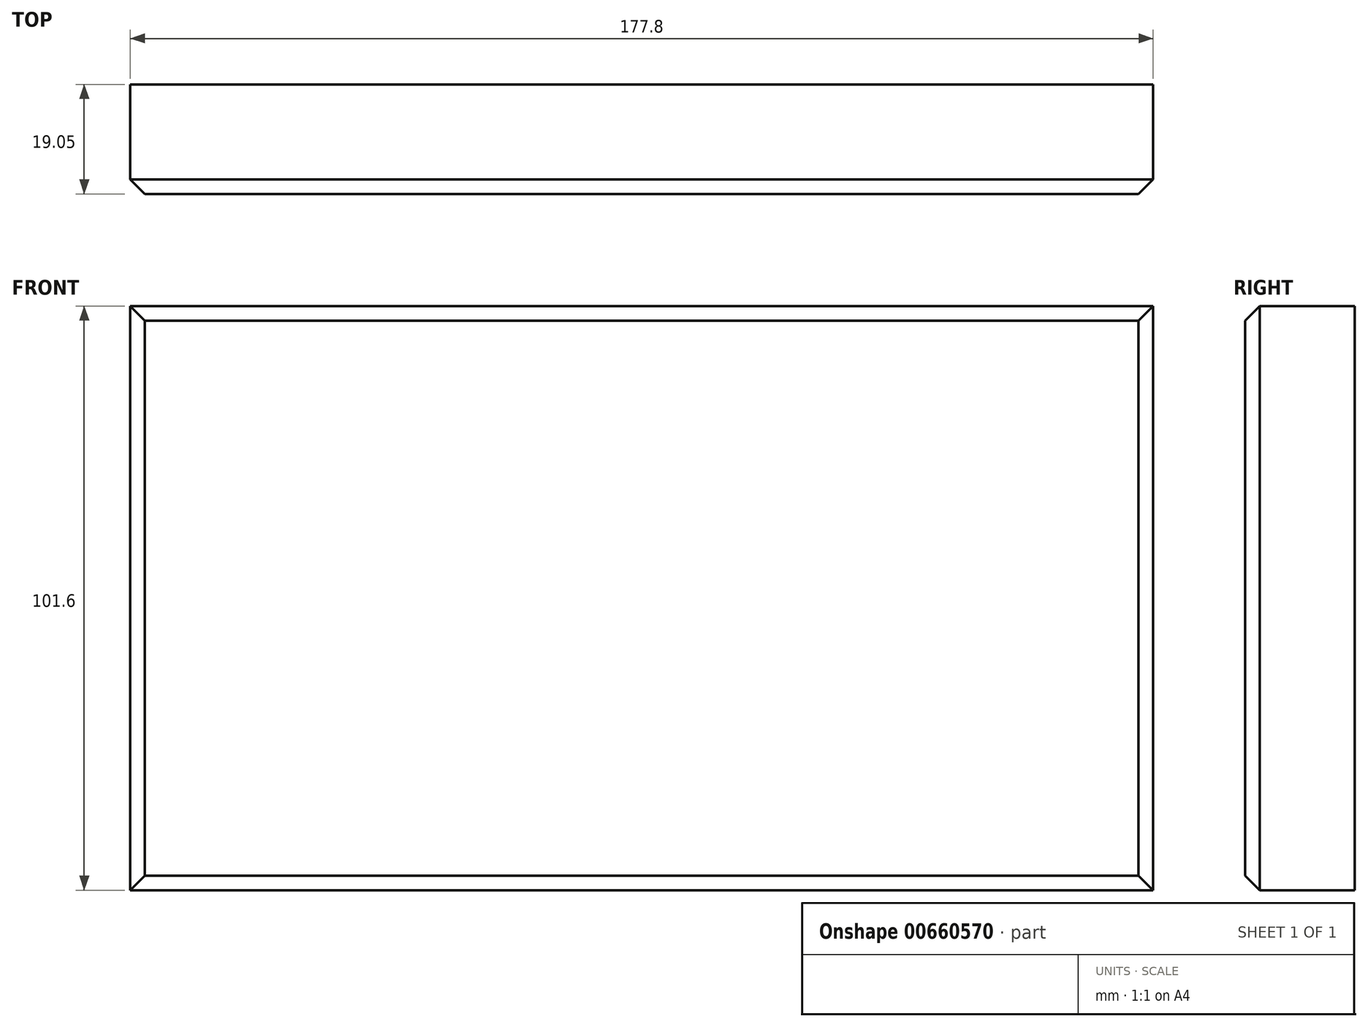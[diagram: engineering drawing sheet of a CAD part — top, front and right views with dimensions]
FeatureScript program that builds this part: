
annotation { "Feature Type Name" : "Feature", "Feature Type Description" : "" }
export const myFeature = defineFeature(function(context is Context, id is Id, definition is map)
    precondition{}
    {
        {
            var Q0;
            Q0=qCreatedBy(makeId("Front.planeOp"),FACE);
            var sketch = newSketch(context, id + "F0", { "sketchPlane" : qUnion([Q0])});
            skLineSegment(sketch, "E0.bottom", {"start": v(-138.09, 54.51) * mm, "end": v(39.71, 54.51) * mm});
            skLineSegment(sketch, "E0.top", {"start": v(-138.09, -47.09) * mm, "end": v(39.71, -47.09) * mm});
            skLineSegment(sketch, "E0.left", {"start": v(-138.09, 54.51) * mm, "end": v(-138.09, -47.09) * mm});
            skLineSegment(sketch, "E0.right", {"start": v(39.71, 54.51) * mm, "end": v(39.71, -47.09) * mm});
            skSolve(sketch);
        }
        {
            var Q0;
            Q0=makeQuery(id+"F0.imprint","IMPRINT",FACE,{"disambiguationData":[TD([[makeQuery(id+"F0.imprint","IMPRINT",EDGE,{"derivedFrom":sQuery(id+"F0.wireOp",EDGE,"E0.bottom")}),-1.0]])]});
            extrude(context, id + "F1", {"entities" : qUnion([Q0]), "depth" : 19.05 * mm, "offsetDistance" : 25.4 * mm});
        }
        {
            var Q0;
            Q0=makeQuery(id+"F1.opExtrude","CAP_EDGE",EDGE,{"disambiguationData":[OSD([sQuery(id+"F0.wireOp",EDGE,"E0.bottom")])],"isStart":false});
            var Q1;
            Q1=makeQuery(id+"F1.opExtrude","CAP_EDGE",EDGE,{"disambiguationData":[OSD([sQuery(id+"F0.wireOp",EDGE,"E0.left")])],"isStart":false});
            var Q2;
            Q2=makeQuery(id+"F1.opExtrude","CAP_EDGE",EDGE,{"disambiguationData":[OSD([sQuery(id+"F0.wireOp",EDGE,"E0.top")])],"isStart":false});
            var Q3;
            Q3=makeQuery(id+"F1.opExtrude","CAP_EDGE",EDGE,{"disambiguationData":[OSD([sQuery(id+"F0.wireOp",EDGE,"E0.right")])],"isStart":false});
            chamfer(context, id + "F2", {"entities" : qUnion([Q0, Q1, Q2, Q3]), "width" : 2.54 * mm, "tangentPropagation" : true});
        }
    });
